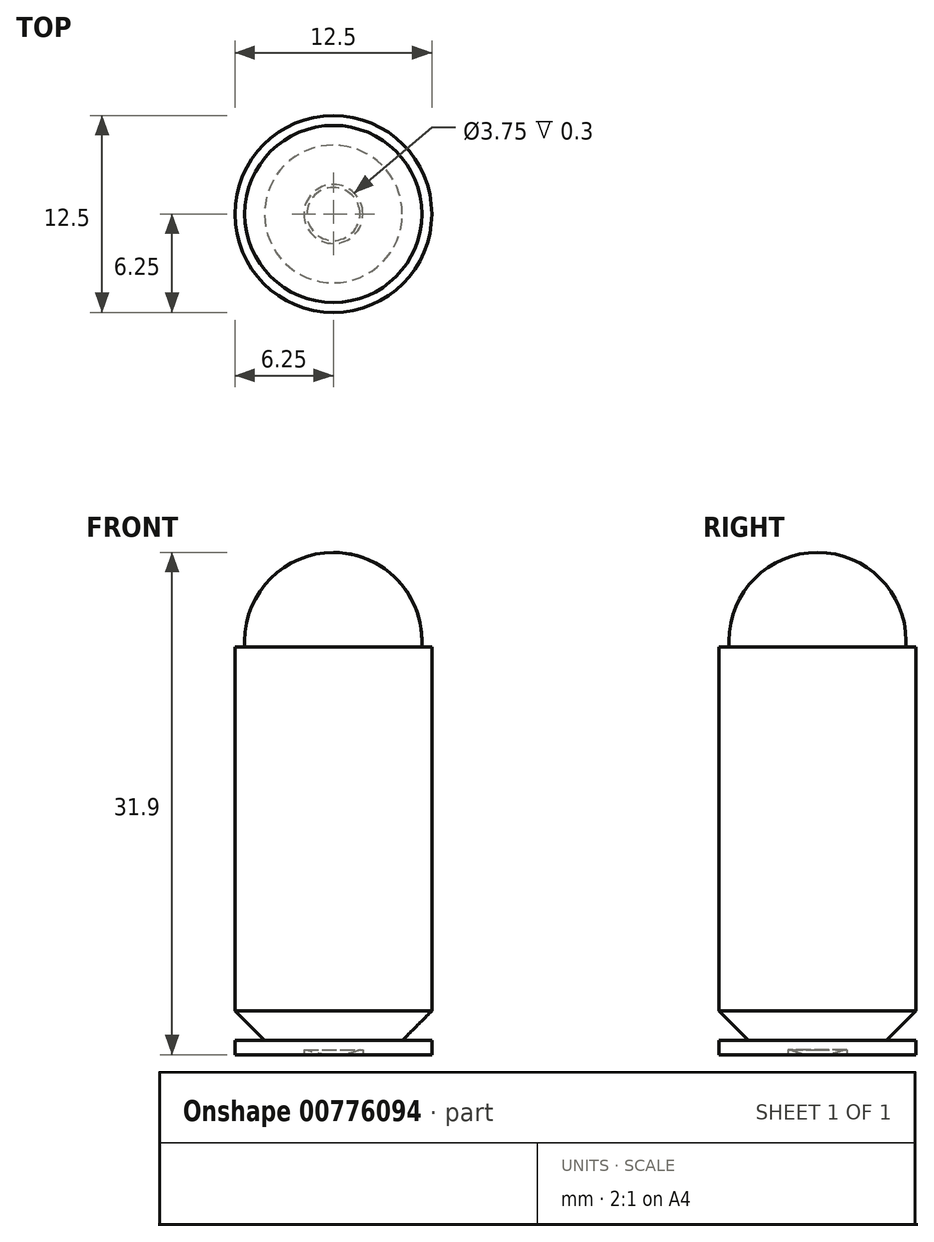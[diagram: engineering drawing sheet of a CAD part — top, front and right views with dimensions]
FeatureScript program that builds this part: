
annotation { "Feature Type Name" : "Feature", "Feature Type Description" : "" }
export const myFeature = defineFeature(function(context is Context, id is Id, definition is map)
    precondition{}
    {
        {
            assignVariable(context, id + "F0", {"name" : "Case", "anyValue" : 12.5});
        }
        {
            var Q0;
            Q0=qCreatedBy(makeId("Top.planeOp"),FACE);
            var sketch = newSketch(context, id + "F1", { "sketchPlane" : qUnion([Q0])});
            skCircle(sketch, "E0", {"center": v(0, 0) * mm, "radius": 6.25 * mm});
            skSolve(sketch);
        }
        {
            var Q0;
            Q0=makeQuery(id+"F1.imprint","IMPRINT",FACE,{"disambiguationData":[TD([[makeQuery(id+"F1.imprint","IMPRINT",EDGE,{"derivedFrom":sQuery(id+"F1.wireOp",EDGE,"E0")}),1.0]])]});
            extrude(context, id + "F2", {"entities" : qUnion([Q0]), "depth" : (2 * getVariable(context, 'Case')) * mm, "offsetDistance" : 25 * mm});
        }
        {
            var Q0;
            Q0=makeQuery(id+"F2.opExtrude","CAP_FACE",FACE,{"disambiguationData":[OSD([sQuery(id+"F1.wireOp",EDGE,"E0")])],"isStart":false});
            var sketch = newSketch(context, id + "F3", { "sketchPlane" : qUnion([Q0])});
            skPoint(sketch, "E1", {"position": v(0, 0) * mm});
            skCircle(sketch, "E2", {"center": v(0, 0) * mm, "radius": 5.62 * mm});
            skSolve(sketch);
        }
        {
            var Q0;
            Q0=makeQuery(id+"F3.imprint","IMPRINT",FACE,{"disambiguationData":[TD([[makeQuery(id+"F3.imprint","IMPRINT",EDGE,{"derivedFrom":sQuery(id+"F3.wireOp",EDGE,"E2")}),1.0]])]});
            extrude(context, id + "F4", {"entities" : qUnion([Q0]), "operationType" : NewBodyOperationType.ADD, "depth" : (.48 * getVariable(context, 'Case')) * mm, "offsetDistance" : 25 * mm});
        }
        {
            var Q0;
            Q0=makeQuery(id+"F4.opExtrude","CAP_EDGE",EDGE,{"disambiguationData":[OSD([sQuery(id+"F3.wireOp",EDGE,"E2")])],"isStart":false});
            fillet(context, id + "F5", {"entities" : qUnion([Q0]), "radius" : (.45 * getVariable(context, 'Case')) * mm, "tangentPropagation" : true, "allowEdgeOverflow" : false});
        }
        {
            var Q0;
            Q0=makeQuery(id+"F2.opExtrude","CAP_EDGE",EDGE,{"disambiguationData":[OSD([sQuery(id+"F1.wireOp",EDGE,"E0")])],"isStart":true});
            chamfer(context, id + "F6", {"entities" : qUnion([Q0]), "width" : (0.15 * getVariable(context, 'Case')) * mm, "tangentPropagation" : true});
        }
        {
            var Q0;
            Q0=makeQuery(id+"F2.opExtrude","CAP_FACE",FACE,{"disambiguationData":[OSD([sQuery(id+"F1.wireOp",EDGE,"E0")])],"isStart":true});
            var sketch = newSketch(context, id + "F7", { "sketchPlane" : qUnion([Q0])});
            skCircle(sketch, "E3", {"center": v(0, 0) * mm, "radius": 6.25 * mm});
            skSolve(sketch);
        }
        {
            var Q0;
            Q0=makeQuery(id+"F7.imprint","IMPRINT",FACE,{"disambiguationData":[TD([[makeQuery(id+"F7.imprint","IMPRINT",EDGE,{"derivedFrom":sQuery(id+"F7.wireOp",EDGE,"E3")}),1.0]])]});
            var Q1;
            {var subQ0=sQuery(id+"F1.wireOp",EDGE,"E0");Q1=makeQuery(id+"F7.imprint","IMPRINT",FACE,{"disambiguationData":[TD([[makeQuery(id+"F7.imprint","IMPRINT",EDGE,{"derivedFrom":makeQuery(id+"F6.opChamfer","BLEND_EDGE",EDGE,{"blendedFrom":[makeQuery(id+"F2.opExtrude","CAP_EDGE",EDGE,{"disambiguationData":[OSD([subQ0])],"isStart":true}),makeQuery(id+"F2.opExtrude","CAP_FACE",FACE,{"disambiguationData":[OSD([subQ0])],"isStart":true})],"blendedInto":[makeQuery(id+"F2.opExtrude","CAP_FACE",FACE,{"disambiguationData":[OSD([subQ0])],"isStart":true})]})}),1.0]])]});}
            extrude(context, id + "F8", {"entities" : qUnion([Q0, Q1]), "operationType" : NewBodyOperationType.ADD, "depth" : 0.9 * mm, "offsetDistance" : 25 * mm});
        }
        {
            var Q0;
            Q0=makeQuery(id+"F8.opExtrude","CAP_FACE",FACE,{"disambiguationData":[OSD([sQuery(id+"F7.wireOp",EDGE,"E3")])],"isStart":false});
            var sketch = newSketch(context, id + "F9", { "sketchPlane" : qUnion([Q0])});
            skCircle(sketch, "E4", {"center": v(0, 0) * mm, "radius": 1.88 * mm});
            skSolve(sketch);
        }
        {
            var Q0;
            Q0 = qSketchRegion(id + "F9", true);
            extrude(context, id + "F10", {"entities" : qUnion([Q0]), "operationType" : NewBodyOperationType.REMOVE, "oppositeDirection" : true, "depth" : .3 * mm, "offsetDistance" : 25 * mm});
        }
        {
            var Q0;
            Q0=makeQuery(id+"F10.boolean.opBoolean","COPY",FACE,{"derivedFrom":makeQuery(id+"F10.opExtrude","CAP_FACE",FACE,{"disambiguationData":[OSD([sQuery(id+"F9.wireOp",EDGE,"E4")])],"isStart":false})});
            var sketch = newSketch(context, id + "F11", { "sketchPlane" : qUnion([Q0])});
            skCircle(sketch, "E5", {"center": v(0, 0) * mm, "radius": 1.69 * mm});
            skSolve(sketch);
        }
        {
            var Q0;
            Q0=makeQuery(id+"F11.imprint","IMPRINT",FACE,{"disambiguationData":[TD([[makeQuery(id+"F11.imprint","IMPRINT",EDGE,{"derivedFrom":sQuery(id+"F11.wireOp",EDGE,"E5")}),1.0]])]});
            extrude(context, id + "F12", {"entities" : qUnion([Q0]), "operationType" : NewBodyOperationType.ADD, "depth" : .3 * mm, "offsetDistance" : 25 * mm});
        }
        {
            var Q0;
            Q0=makeQuery(id+"F12.opExtrude","CAP_FACE",FACE,{"disambiguationData":[OSD([sQuery(id+"F11.wireOp",EDGE,"E5")])],"isStart":false});
            fillet(context, id + "F13", {"entities" : qUnion([Q0]), "radius" : (.3 * getVariable(context, 'Case')) * mm, "tangentPropagation" : true, "allowEdgeOverflow" : false});
        }
    });
